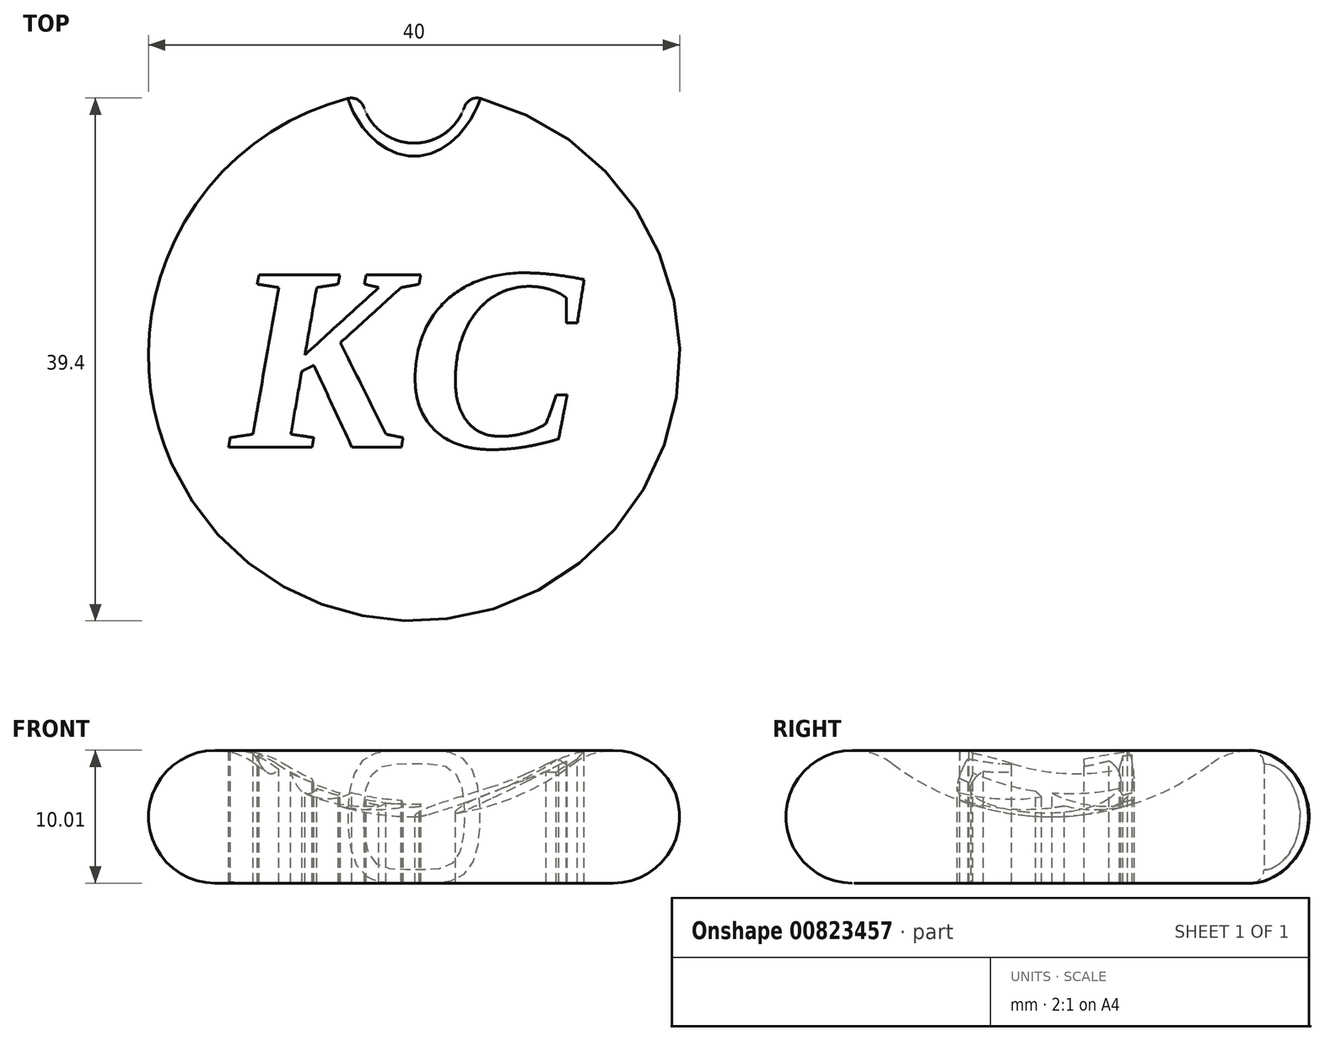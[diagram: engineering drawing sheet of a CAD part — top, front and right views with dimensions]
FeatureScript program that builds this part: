
annotation { "Feature Type Name" : "Feature", "Feature Type Description" : "" }
export const myFeature = defineFeature(function(context is Context, id is Id, definition is map)
    precondition{}
    {
        {
            var Q0;
            Q0=qCreatedBy(makeId("Front.planeOp"),FACE);
            var sketch = newSketch(context, id + "F0", { "sketchPlane" : qUnion([Q0])});
            skArc(sketch, "E0", {"start": v(-12, 9) * mm, "mid": v(-19.74, 6.58) * mm, "end": v(-15, 0) * mm});
            skArc(sketch, "E1", {"start": v(-12, 9) * mm, "mid": v(-6.32, 6.03) * mm, "end": v(0, 5) * mm});
            skLineSegment(sketch, "E2", {"start": v(0, 0) * mm, "end": v(-15, 0) * mm});
            skLineSegment(sketch, "E3", {"start": v(0, 0) * mm, "end": v(0, 5) * mm});
            skSolve(sketch);
        }
        {
            var Q0;
            Q0=makeQuery(id+"F0.imprint","IMPRINT",FACE,{"disambiguationData":[TD([[makeQuery(id+"F0.imprint","IMPRINT",EDGE,{"derivedFrom":sQuery(id+"F0.wireOp",EDGE,"E0")}),1.0]])]});
            var Q1;
            Q1=sQuery(id+"F0.wireOp",EDGE,"E3");
            revolve(context, id + "F1", {"surfaceOperationType" : NewSurfaceOperationType.NEW, "entities" : qUnion([Q0]), "axis" : qUnion([Q1]), "revolveType" : RevolveType.FULL});
        }
        {
            var Q0;
            Q0=qCreatedBy(makeId("Top.planeOp"),FACE);
            cPlane(context, id + "F2", {"entities" : qUnion([Q0]), "cplaneType" : CPlaneType.OFFSET, "offset" : 10 * mm, "width" : 150 * mm, "height" : 150 * mm});
        }
        {
            var Q0;
            Q0=qCreatedBy(id+"F2.planeOp",FACE);
            var sketch = newSketch(context, id + "F3", { "sketchPlane" : qUnion([Q0])});
            skText(sketch, "E4", { "text": "KC", "fontName": "Tinos-BoldItalic.ttf"});
            const initialGuessF3  = {"E4": [-0.01382, -0.0069, 1, 0, 0.01427]};
            skSetInitialGuess(sketch, initialGuessF3);
            skSolve(sketch);
        }
        {
            var Q0;
            Q0 = qSketchRegion(id + "F3", true);
            extrude(context, id + "F4", {"entities" : qUnion([Q0]), "operationType" : NewBodyOperationType.REMOVE, "oppositeDirection" : true, "depth" : 25 * mm, "offsetDistance" : 25 * mm});
        }
        {
            var Q0;
            Q0=qCreatedBy(makeId("Front.planeOp"),FACE);
            var sketch = newSketch(context, id + "F5", { "sketchPlane" : qUnion([Q0])});
            skSolve(sketch);
        }
        {
            var Q0;
            Q0=qCreatedBy(makeId("Top.planeOp"),FACE);
            var sketch = newSketch(context, id + "F6", { "sketchPlane" : qUnion([Q0])});
            skCircle(sketch, "E5", {"center": v(0, 20) * mm, "radius": 4 * mm});
            skSolve(sketch);
        }
        {
            var Q0;
            Q0=makeQuery(id+"F6.imprint","IMPRINT",FACE,{"disambiguationData":[TD([[makeQuery(id+"F6.imprint","IMPRINT",EDGE,{"derivedFrom":sQuery(id+"F6.wireOp",EDGE,"E5")}),1.0]])]});
            var Q1;
            Q1 = qSketchRegion(id + "F5", true);
            extrude(context, id + "F7", {"entities" : qUnion([Q0, Q1]), "operationType" : NewBodyOperationType.REMOVE, "endBound" : BoundingType.SYMMETRIC, "depth" : 25 * mm, "offsetDistance" : 25 * mm});
        }
        {
            var Q0;
            Q0=makeQuery(id+"F7.boolean.opBoolean","INTERSECT",EDGE,{"derivedFrom":[makeQuery(id+"F4.boolean.opBoolean","SPLIT",FACE,{"disambiguationData":[TD([makeQuery(id+"F1.opRevolve","SWEPT_FACE",FACE,{"disambiguationData":[OSD([sQuery(id+"F0.wireOp",EDGE,"E2")])]})])],"derivedFrom":makeQuery(id+"F1.opRevolve","SWEPT_FACE",FACE,{"disambiguationData":[OSD([sQuery(id+"F0.wireOp",EDGE,"E0")])]})}),makeQuery(id+"F7.opExtrude","SWEPT_FACE",FACE,{"disambiguationData":[OSD([sQuery(id+"F6.wireOp",EDGE,"E5")])]})]});
            fillet(context, id + "F8", {"entities" : qUnion([Q0]), "radius" : 1 * mm, "tangentPropagation" : true, "allowEdgeOverflow" : false});
        }
    });
